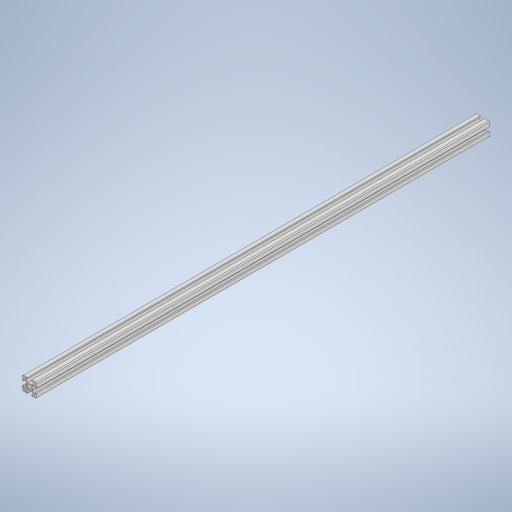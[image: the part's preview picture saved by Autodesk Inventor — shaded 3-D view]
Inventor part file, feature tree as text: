
AUTODESK INVENTOR PART (.ipt)
format: ipt  version: 2023.2 (Build 272271030, 271C)  size: 330,240 bytes
history: native  units: mm
features: extrude x1, fillet x1, sketch x1
ambient origin geometry x8: Origin, YZ Plane, XZ Plane, XY Plane, X Axis, Y Axis, Z Axis, Center Point
bodies: Solid1 (feature_tree)
feature tree (3):
  extrude  "Extrusion1"  Depth=20.0mm
  fillet  "Fillet1"  Radius=5.0mm
  sketch  "Sketch1"  dims[d8=20.0mm d9=20.0mm d10=5.0mm d18=6.1mm d19=6.1mm d21=1.5mm d24=4.5mm d25=4.5mm d26=1.5mm d27=6.9mm d28=1.8mm d29=651.0mm d30=0.0mm d31=1.5mm]
